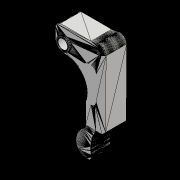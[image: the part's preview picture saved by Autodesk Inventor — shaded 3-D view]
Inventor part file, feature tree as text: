
AUTODESK INVENTOR PART (.ipt)
format: ipt  version: 2018.2 (Build 222227000, 227)  size: 6,852,608 bytes
history: native  units: mm
features: extrude x5, sketch x4, other x1, chamfer x1, imported_body x1
ambient origin geometry x8: Origin, YZ Plane, XZ Plane, XY Plane, X Axis, Y Axis, Z Axis, Center Point
bodies: Body1 (feature_tree)
feature tree (12):
  other  "ソリッド1"
  extrude  "押し出し1"  Depth=4.5mm
  extrude  "押し出し2"  Depth=5.0mm TaperAngle=0.0deg
  extrude  "押し出し3"  Depth=8.0mm
  chamfer  "面取り1"  Distance=0.75mm
  sketch  "スケッチ4"
  extrude  "押し出し4"  Depth=5.0mm TaperAngle=0.0deg
  extrude  "押し出し5"  Depth=5.5mm
  sketch  "スケッチ1"
  sketch  "スケッチ2"
  sketch  "スケッチ3"
  imported_body  "Base1"
